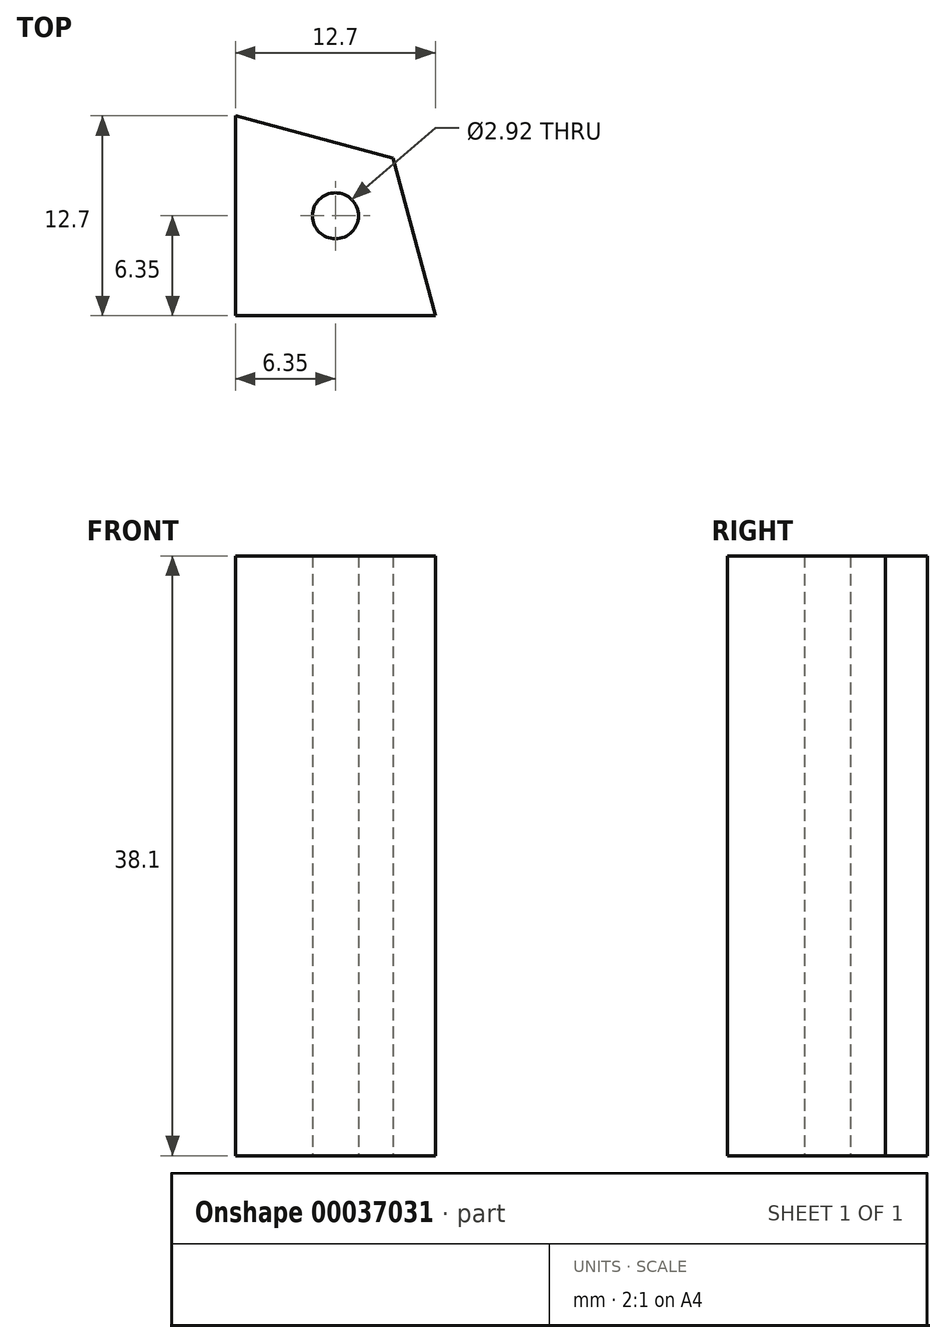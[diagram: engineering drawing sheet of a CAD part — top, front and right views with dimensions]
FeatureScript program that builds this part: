
annotation { "Feature Type Name" : "Feature", "Feature Type Description" : "" }
export const myFeature = defineFeature(function(context is Context, id is Id, definition is map)
    precondition{}
    {
        {
            var Q0;
            Q0=qCreatedBy(makeId("Top.planeOp"),FACE);
            var sketch = newSketch(context, id + "F0", { "sketchPlane" : qUnion([Q0])});
            skLineSegment(sketch, "E0.rect.bottom", {"start": v(6.35, 6.35) * mm, "end": v(-6.35, 6.35) * mm, "construction": true});
            skLineSegment(sketch, "E0.rect.top", {"start": v(6.35, -6.35) * mm, "end": v(-6.35, -6.35) * mm});
            skLineSegment(sketch, "E0.rect.left", {"start": v(6.35, 6.35) * mm, "end": v(6.35, -6.35) * mm, "construction": true});
            skLineSegment(sketch, "E0.rect.right", {"start": v(-6.35, 6.35) * mm, "end": v(-6.35, -6.35) * mm});
            skPoint(sketch, "E0.rect.middle", {"position": v(0, 0) * mm});
            skLineSegment(sketch, "E1", {"start": v(-6.35, 6.35) * mm, "end": v(3.67, 3.67) * mm});
            skLineSegment(sketch, "E2", {"start": v(3.67, 3.67) * mm, "end": v(6.35, -6.35) * mm});
            skLineSegment(sketch, "E3", {"start": v(-6.35, -6.35) * mm, "end": v(6.35, 6.35) * mm, "construction": true});
            skCircle(sketch, "E4", {"center": v(0, 0) * mm, "radius": 1.46 * mm});
            skSolve(sketch);
        }
        {
            var Q0;
            Q0=makeQuery(id+"F0.imprint","IMPRINT",FACE,{"disambiguationData":[TD([[makeQuery(id+"F0.imprint","IMPRINT",EDGE,{"derivedFrom":sQuery(id+"F0.wireOp",EDGE,"E0.rect.top")}),-1.0]])]});
            extrude(context, id + "F1", {"entities" : qUnion([Q0]), "endBound" : BoundingType.SYMMETRIC, "depth" : 38.1 * mm + 1 / 203.2 * mm});
        }
    });
